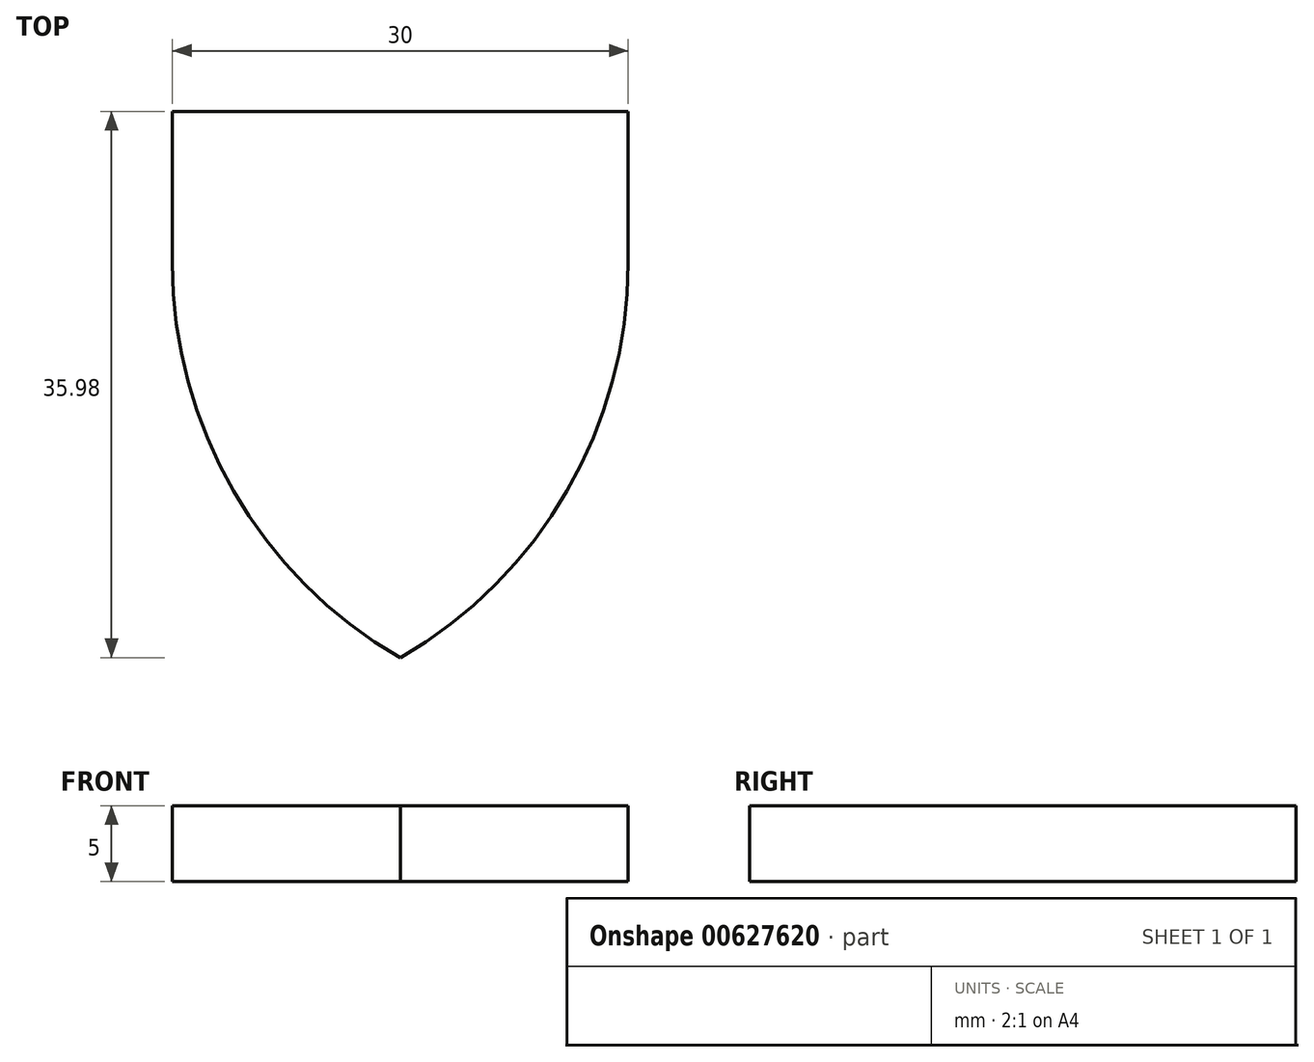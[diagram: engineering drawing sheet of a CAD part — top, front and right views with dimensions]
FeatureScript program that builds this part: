
annotation { "Feature Type Name" : "Feature", "Feature Type Description" : "" }
export const myFeature = defineFeature(function(context is Context, id is Id, definition is map)
    precondition{}
    {
        {
            var Q0;
            Q0=qCreatedBy(makeId("Top.planeOp"),FACE);
            var sketch = newSketch(context, id + "F0", { "sketchPlane" : qUnion([Q0])});
            skLineSegment(sketch, "E0.top", {"start": v(0, 15) * mm, "end": v(-15, 15) * mm});
            skLineSegment(sketch, "E0.left", {"start": v(0, 0) * mm, "end": v(0, 15) * mm});
            skLineSegment(sketch, "E0.right", {"start": v(-15, 5) * mm, "end": v(-15, 15) * mm});
            skLineSegment(sketch, "E1.MirrorCS", {"start": v(0, 15) * mm, "end": v(15, 15) * mm});
            skLineSegment(sketch, "E2", {"start": v(15, 15) * mm, "end": v(15, 5) * mm});
            skArc(sketch, "E3", {"start": v(0, -20.98) * mm, "mid": v(10.98, -10) * mm, "end": v(15, 5) * mm});
            skArc(sketch, "E4", {"start": v(-15, 5) * mm, "mid": v(-10.98, -10) * mm, "end": v(0, -20.98) * mm});
            skSolve(sketch);
        }
        {
            var Q0;
            Q0=makeQuery(id+"F0.imprint","IMPRINT",FACE,{"disambiguationData":[TD([[makeQuery(id+"F0.imprint","IMPRINT",EDGE,{"derivedFrom":sQuery(id+"F0.wireOp",EDGE,"E0.top")}),1.0]])]});
            extrude(context, id + "F1", {"entities" : qUnion([Q0]), "depth" : 5 * mm, "offsetDistance" : 25 * mm});
        }
    });
